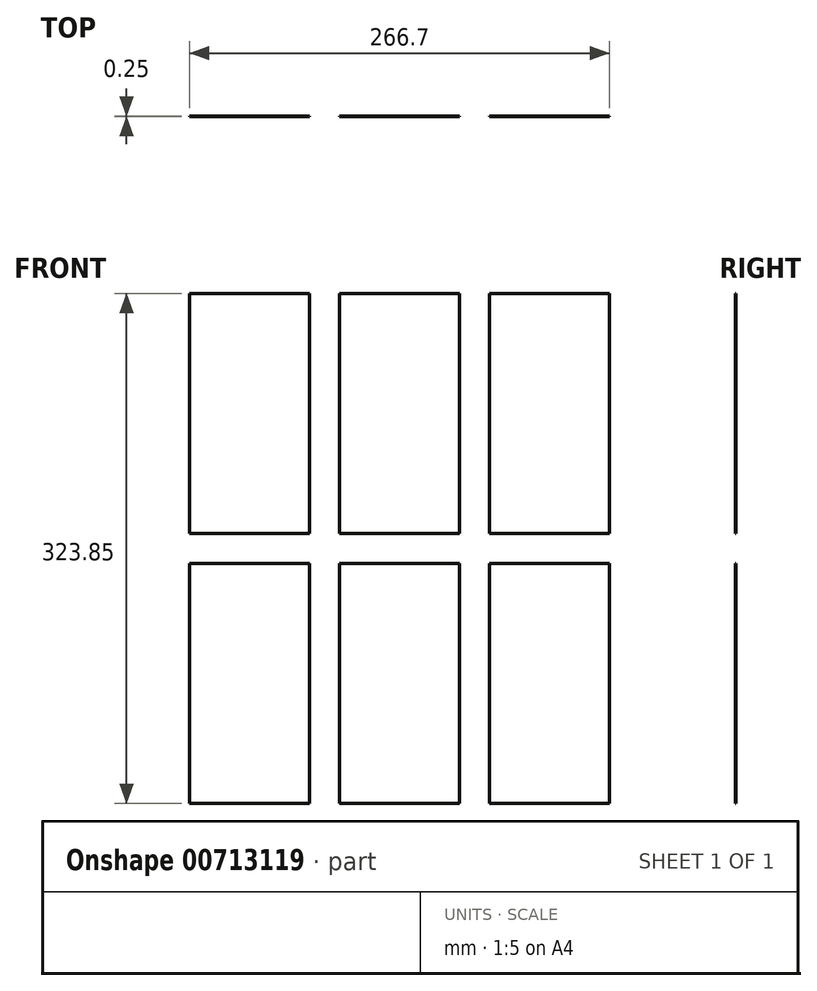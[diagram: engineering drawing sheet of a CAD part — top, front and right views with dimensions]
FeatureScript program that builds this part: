
annotation { "Feature Type Name" : "Feature", "Feature Type Description" : "" }
export const myFeature = defineFeature(function(context is Context, id is Id, definition is map)
    precondition{}
    {
        {
            var Q0;
            Q0=qCreatedBy(makeId("Front.planeOp"),FACE);
            var sketch = newSketch(context, id + "F0", { "sketchPlane" : qUnion([Q0])});
            skLineSegment(sketch, "E0.bottom", {"start": v(0, 0) * mm, "end": v(76.2, 0) * mm});
            skLineSegment(sketch, "E0.top", {"start": v(0, -152.4) * mm, "end": v(76.2, -152.4) * mm});
            skLineSegment(sketch, "E0.left", {"start": v(0, 0) * mm, "end": v(0, -152.4) * mm});
            skLineSegment(sketch, "E0.right", {"start": v(76.2, 0) * mm, "end": v(76.2, -152.4) * mm});
            skLineSegment(sketch, "E1.0.1.0", {"start": v(76.2, -171.45) * mm, "end": v(76.2, -323.85) * mm});
            skLineSegment(sketch, "E1.0.1.1", {"start": v(0, -171.45) * mm, "end": v(76.2, -171.45) * mm});
            skLineSegment(sketch, "E1.0.1.2", {"start": v(0, -171.45) * mm, "end": v(0, -323.85) * mm});
            skLineSegment(sketch, "E1.0.1.3", {"start": v(0, -323.85) * mm, "end": v(76.2, -323.85) * mm});
            skLineSegment(sketch, "E1.1.0.0", {"start": v(171.45, 0) * mm, "end": v(171.45, -152.4) * mm});
            skLineSegment(sketch, "E1.1.0.1", {"start": v(95.25, 0) * mm, "end": v(171.45, 0) * mm});
            skLineSegment(sketch, "E1.1.0.2", {"start": v(95.25, 0) * mm, "end": v(95.25, -152.4) * mm});
            skLineSegment(sketch, "E1.1.0.3", {"start": v(95.25, -152.4) * mm, "end": v(171.45, -152.4) * mm});
            skLineSegment(sketch, "E1.1.1.0", {"start": v(171.45, -171.45) * mm, "end": v(171.45, -323.85) * mm});
            skLineSegment(sketch, "E1.1.1.1", {"start": v(95.25, -171.45) * mm, "end": v(171.45, -171.45) * mm});
            skLineSegment(sketch, "E1.1.1.2", {"start": v(95.25, -171.45) * mm, "end": v(95.25, -323.85) * mm});
            skLineSegment(sketch, "E1.1.1.3", {"start": v(95.25, -323.85) * mm, "end": v(171.45, -323.85) * mm});
            skLineSegment(sketch, "E1.2.0.0", {"start": v(266.7, 0) * mm, "end": v(266.7, -152.4) * mm});
            skLineSegment(sketch, "E1.2.0.1", {"start": v(190.5, 0) * mm, "end": v(266.7, 0) * mm});
            skLineSegment(sketch, "E1.2.0.2", {"start": v(190.5, 0) * mm, "end": v(190.5, -152.4) * mm});
            skLineSegment(sketch, "E1.2.0.3", {"start": v(190.5, -152.4) * mm, "end": v(266.7, -152.4) * mm});
            skLineSegment(sketch, "E1.2.1.0", {"start": v(266.7, -171.45) * mm, "end": v(266.7, -323.85) * mm});
            skLineSegment(sketch, "E1.2.1.1", {"start": v(190.5, -171.45) * mm, "end": v(266.7, -171.45) * mm});
            skLineSegment(sketch, "E1.2.1.2", {"start": v(190.5, -171.45) * mm, "end": v(190.5, -323.85) * mm});
            skLineSegment(sketch, "E1.2.1.3", {"start": v(190.5, -323.85) * mm, "end": v(266.7, -323.85) * mm});
            skLineSegment(sketch, "E1.direction2", {"start": v(0, -152.4) * mm, "end": v(0, -323.85) * mm, "construction": true});
            skSolve(sketch);
        }
        {
            var Q0;
            Q0=makeQuery(id+"F0.imprint","IMPRINT",FACE,{"disambiguationData":[TD([[makeQuery(id+"F0.imprint","IMPRINT",EDGE,{"derivedFrom":sQuery(id+"F0.wireOp",EDGE,"E0.bottom")}),-1.0]])]});
            var Q1;
            Q1=makeQuery(id+"F0.imprint","IMPRINT",FACE,{"disambiguationData":[TD([[makeQuery(id+"F0.imprint","IMPRINT",EDGE,{"derivedFrom":sQuery(id+"F0.wireOp",EDGE,"E1.0.1.0")}),-1.0]])]});
            var Q2;
            Q2=makeQuery(id+"F0.imprint","IMPRINT",FACE,{"disambiguationData":[TD([[makeQuery(id+"F0.imprint","IMPRINT",EDGE,{"derivedFrom":sQuery(id+"F0.wireOp",EDGE,"E1.1.0.0")}),-1.0]])]});
            var Q3;
            Q3=makeQuery(id+"F0.imprint","IMPRINT",FACE,{"disambiguationData":[TD([[makeQuery(id+"F0.imprint","IMPRINT",EDGE,{"derivedFrom":sQuery(id+"F0.wireOp",EDGE,"E1.1.1.0")}),-1.0]])]});
            var Q4;
            Q4=makeQuery(id+"F0.imprint","IMPRINT",FACE,{"disambiguationData":[TD([[makeQuery(id+"F0.imprint","IMPRINT",EDGE,{"derivedFrom":sQuery(id+"F0.wireOp",EDGE,"E1.2.0.0")}),-1.0]])]});
            var Q5;
            Q5=makeQuery(id+"F0.imprint","IMPRINT",FACE,{"disambiguationData":[TD([[makeQuery(id+"F0.imprint","IMPRINT",EDGE,{"derivedFrom":sQuery(id+"F0.wireOp",EDGE,"E1.2.1.0")}),-1.0]])]});
            extrude(context, id + "F1", {"entities" : qUnion([Q0, Q1, Q2, Q3, Q4, Q5]), "depth" : 0.25 * mm, "offsetDistance" : 25.4 * mm});
        }
    });
